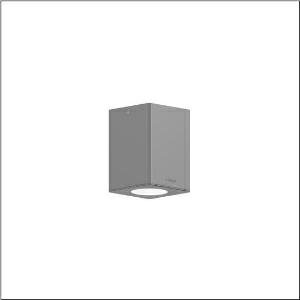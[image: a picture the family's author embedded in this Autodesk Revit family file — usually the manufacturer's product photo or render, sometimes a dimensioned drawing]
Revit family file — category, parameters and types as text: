
# Revit family: cl_31_decke_5cl613603
name_source: partatom
category: Lighting Fixtures
units: mm (PartAtom-declared; Revit-internal decimal feet)

## family parameters
Cut with Voids When Loaded = No
Host = Face
Light Source = No
Part Type = Normal
Room Calculation Point = No
Round Connector Dimension = Use Diameter
Shared = No

## types (1)
- --- (1 x LED, 1500 lm, 15 W, 3000K)
    Apparent Load = 15 VA
    CIE Flux Codes = 98 100 100 100 100
    Color Rendering = 80
    Color Temperature = 3000K
    Default Elevation = 1800 mm
    Description = CL 31 Ceiling, ceiling luminaire, primary light control with reflector, of aluminium, primary optical cover: cover panel, of glass, transparent, primary light characteristic: symmetric, installation type: surface-mounted, LED, rated luminous flux: 1.500lm, luminous efficacy: 100lm/W, light colour: 830, colour temperature: 3000K, control gear: ECG DALI, with terminal, 5-pole, max. 2.5mm², mains connection: 220..240V, AC, 50/60Hz, rated input power: 15W, luminaire housing, of aluminium, powder-coated, Siteco® metallic grey, length: 120mm, width: 120mm, height: 165mm, protection rating (complete): IP65, insulation class (complete): insulation class I (protective earthing), certification: CE, ENEC, impact resistance: IK09, permissible operating ambient temperature for outdoor applications: -20..+50°C, packaging unit: 1 piece
    Height = 166 mm
    Lamp = 1 x LED
    Lamp Light Flux = 1500 lm
    Lamp Power = 15 W
    Lamp count = 1
    Length = 120 mm
    Luminous efficacy = 100 lm/W
    Manufacturer = Siteco
    ModVariant = No
    Model = 5CL613603
    Mounting Place = Ceiling
    Mounting Type = Surface mounted
    Number of Poles = 1
    OnlyDefault = Yes
    Power Factor = 1
    Product Name = CL 31 Decke
    Product group = ceiling luminaire
    ProductGroupID = 305
    Protection Class = Protection class I
    Protection Degree = IP 65
    RLX_Detail_Level = 1
    RLX_Emergency_Light_Flux = 0 lm
    RLX_Emergency_Type = 0
    RLX_Emergency_Type_DB = No
    RlxData = <blob elided: 33165 chars, md5=4d41929a>
    Socket = socket
    Standby Power = 0 W
    System Light Flux = 1500 lm
    System Power = 15 W
    Type Comments = factory setting: luminous flux: 100 % | dim-lin: 254 | 348 mA
    Type Image = l_1006909.jpg
    URL = http://relux.com
    VarID = @adj_148577
    Voltage = 0 V
    Weight = 0.00 kg
    Width = 120 mm

## geometry (parser evidence)
native form markers: Blend x4, Sweep x10
no freeform markers — native parametric forms only
